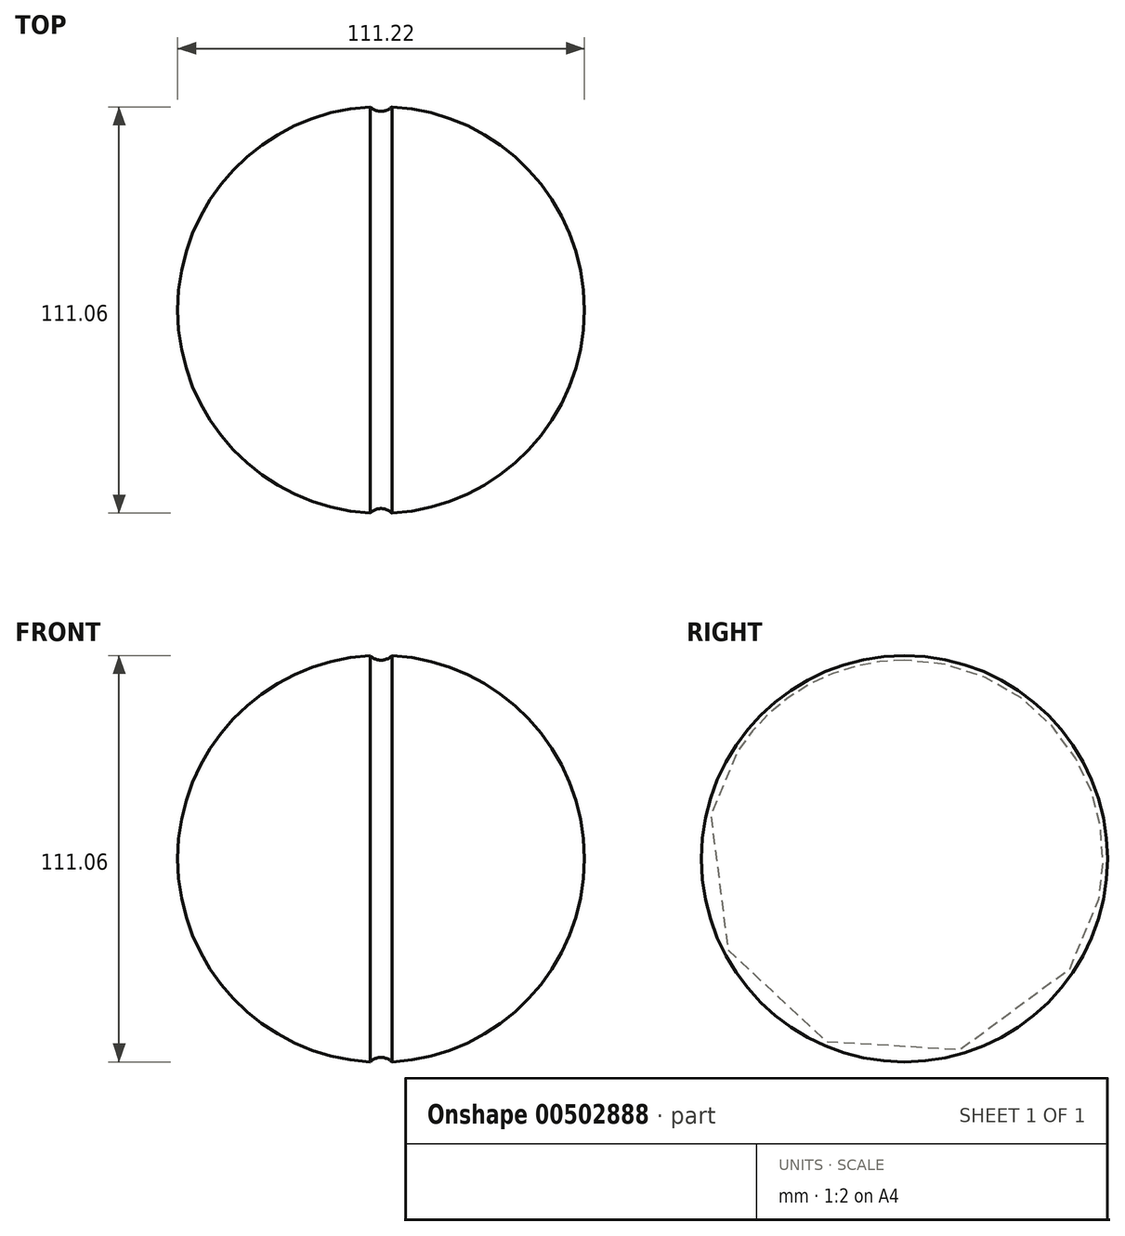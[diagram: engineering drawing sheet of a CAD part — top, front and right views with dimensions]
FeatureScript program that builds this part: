
annotation { "Feature Type Name" : "Feature", "Feature Type Description" : "" }
export const myFeature = defineFeature(function(context is Context, id is Id, definition is map)
    precondition{}
    {
        {
            var Q0;
            Q0=qCreatedBy(makeId("Front.planeOp"),FACE);
            var sketch = newSketch(context, id + "F0", { "sketchPlane" : qUnion([Q0])});
            skArc(sketch, "E0", {"start": v(0, 55.61) * mm, "mid": v(-55.61, 0) * mm, "end": v(0, -55.61) * mm});
            skLineSegment(sketch, "E1", {"start": v(0, 55.61) * mm, "end": v(0, -55.61) * mm});
            skSolve(sketch);
        }
        {
            var Q0;
            Q0 = qSketchRegion(id + "F0", true);
            var Q1;
            Q1=sQuery(id+"F0.wireOp",EDGE,"E1");
            revolve(context, id + "F1", {"entities" : qUnion([Q0]), "axis" : qUnion([Q1]), "revolveType" : RevolveType.FULL});
        }
        {
            var Q0;
            Q0=qCreatedBy(makeId("Front.planeOp"),FACE);
            var sketch = newSketch(context, id + "F2", { "sketchPlane" : qUnion([Q0])});
            skCircle(sketch, "E2", {"center": v(0, 58.63) * mm, "radius": 4.32 * mm});
            skLineSegment(sketch, "E3", {"start": v(0, 0) * mm, "end": v(-74.1, 0) * mm, "construction": true});
            skSolve(sketch);
        }
        {
            var Q0;
            Q0 = qSketchRegion(id + "F2", true);
            var Q1;
            Q1=sQuery(id+"F2.wireOp",EDGE,"E3");
            revolve(context, id + "F3", {"operationType" : NewBodyOperationType.REMOVE, "entities" : qUnion([Q0]), "axis" : qUnion([Q1]), "revolveType" : RevolveType.FULL, "oppositeDirection" : true});
        }
    });
